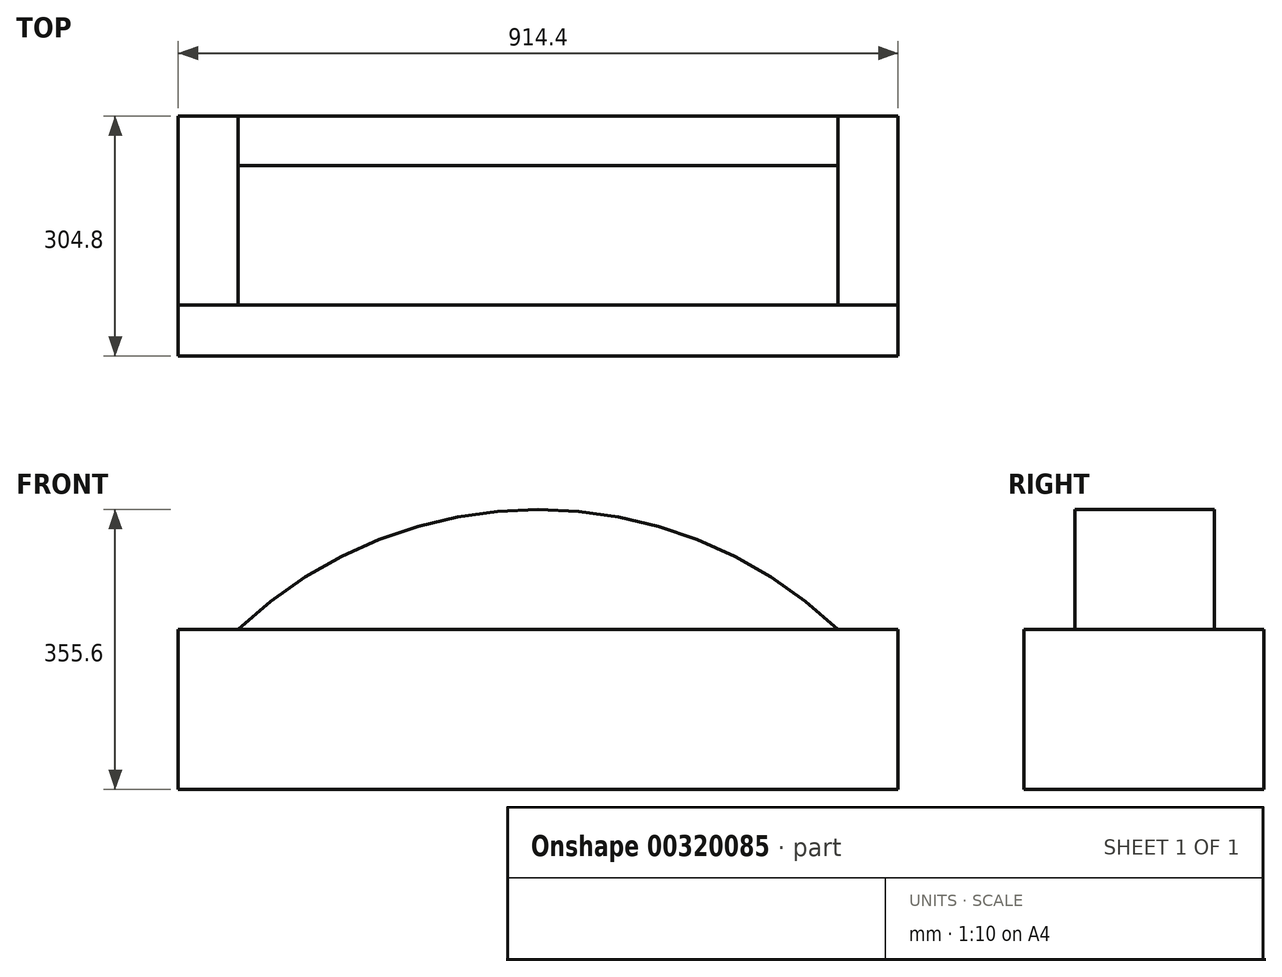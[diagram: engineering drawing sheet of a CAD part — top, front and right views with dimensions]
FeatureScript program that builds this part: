
annotation { "Feature Type Name" : "Feature", "Feature Type Description" : "" }
export const myFeature = defineFeature(function(context is Context, id is Id, definition is map)
    precondition{}
    {
        {
            var Q0;
            Q0=qCreatedBy(makeId("Front.planeOp"),FACE);
            var sketch = newSketch(context, id + "F0", { "sketchPlane" : qUnion([Q0])});
            skLineSegment(sketch, "E0.bottom", {"start": v(457.2, 101.6) * mm, "end": v(-457.2, 101.6) * mm});
            skLineSegment(sketch, "E0.top", {"start": v(457.2, -101.6) * mm, "end": v(-457.2, -101.6) * mm});
            skLineSegment(sketch, "E0.left", {"start": v(457.2, 101.6) * mm, "end": v(457.2, -101.6) * mm});
            skLineSegment(sketch, "E0.right", {"start": v(-457.2, 101.6) * mm, "end": v(-457.2, -101.6) * mm});
            skPoint(sketch, "E0.middle", {"position": v(0, 0) * mm});
            skArc(sketch, "E1", {"start": v(381, 101.6) * mm, "mid": v(0, 254) * mm, "end": v(-381, 101.6) * mm});
            skSolve(sketch);
        }
        {
            var Q0;
            Q0 = qSketchRegion(id + "F0", true);
            extrude(context, id + "F1", {"entities" : qUnion([Q0]), "depth" : 304.8 * mm});
        }
        {
            var Q0;
            Q0=qCreatedBy(makeId("Right.planeOp"),FACE);
            var sketch = newSketch(context, id + "F2", { "sketchPlane" : qUnion([Q0])});
            skLineSegment(sketch, "E2.bottom", {"start": v(0, 101.63) * mm, "end": v(-62.78, 101.63) * mm});
            skLineSegment(sketch, "E2.top", {"start": v(0, 344.51) * mm, "end": v(-62.78, 344.51) * mm});
            skLineSegment(sketch, "E2.left", {"start": v(0, 101.63) * mm, "end": v(0, 344.51) * mm});
            skLineSegment(sketch, "E2.right", {"start": v(-62.78, 101.63) * mm, "end": v(-62.78, 344.51) * mm});
            skLineSegment(sketch, "E3.bottom", {"start": v(-322.38, 101.58) * mm, "end": v(-240.21, 101.58) * mm});
            skLineSegment(sketch, "E3.top", {"start": v(-322.38, 352.85) * mm, "end": v(-240.21, 352.85) * mm});
            skLineSegment(sketch, "E3.left", {"start": v(-322.38, 101.58) * mm, "end": v(-322.38, 352.85) * mm});
            skLineSegment(sketch, "E3.right", {"start": v(-240.21, 101.58) * mm, "end": v(-240.21, 352.85) * mm});
            skSolve(sketch);
        }
        {
            var Q0;
            Q0 = qSketchRegion(id + "F2", true);
            extrude(context, id + "F3", {"entities" : qUnion([Q0]), "operationType" : NewBodyOperationType.REMOVE, "depth" : 914.4 * mm, "hasSecondDirection" : true, "secondDirectionOppositeDirection" : true, "secondDirectionDepth" : 457.2 * mm});
        }
    });
